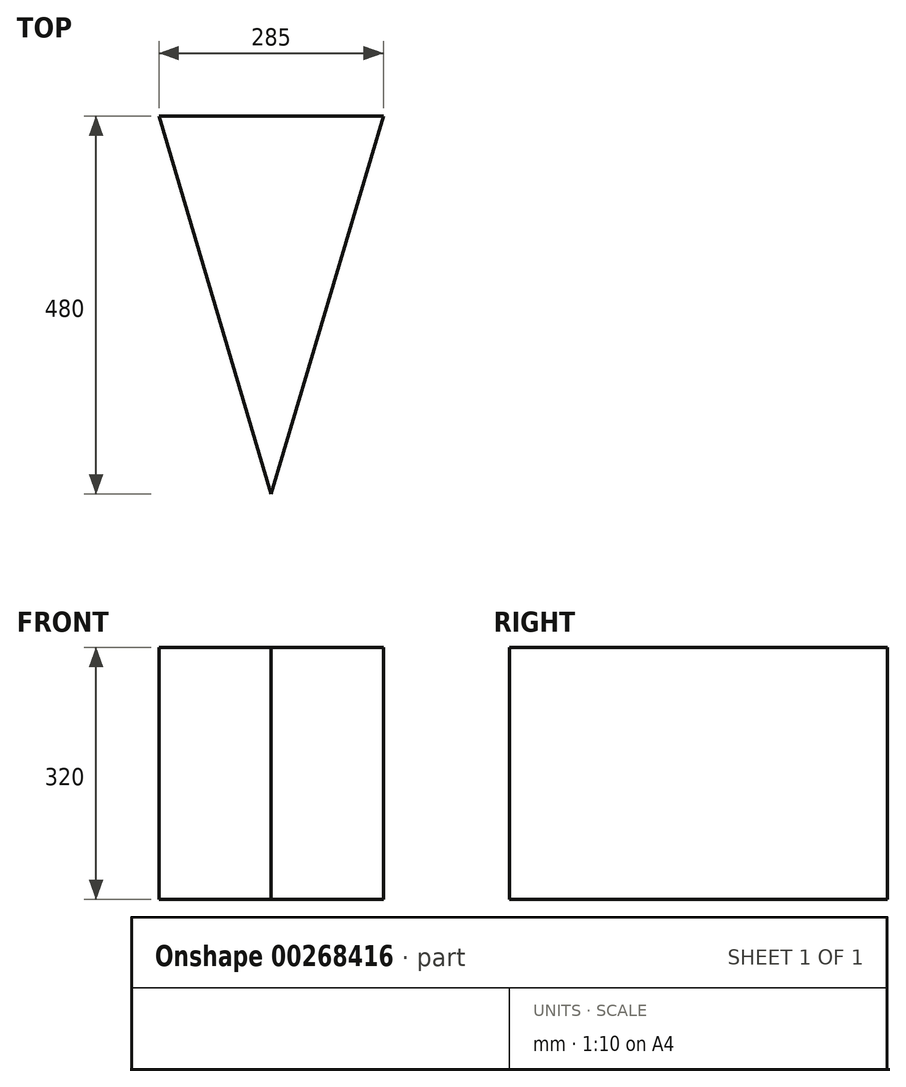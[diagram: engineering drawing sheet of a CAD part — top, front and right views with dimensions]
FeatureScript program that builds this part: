
annotation { "Feature Type Name" : "Feature", "Feature Type Description" : "" }
export const myFeature = defineFeature(function(context is Context, id is Id, definition is map)
    precondition{}
    {
        {
            var Q0;
            Q0=qCreatedBy(makeId("Top.planeOp"),FACE);
            var sketch = newSketch(context, id + "F0", { "sketchPlane" : qUnion([Q0])});
            skLineSegment(sketch, "E0.bottom", {"start": v(142.5, 240) * mm, "end": v(-142.5, 240) * mm});
            skLineSegment(sketch, "E0.top", {"start": v(142.5, -240) * mm, "end": v(-142.5, -240) * mm, "construction": true});
            skLineSegment(sketch, "E0.left", {"start": v(142.5, 240) * mm, "end": v(142.5, -240) * mm, "construction": true});
            skLineSegment(sketch, "E0.right", {"start": v(-142.5, 240) * mm, "end": v(-142.5, -240) * mm, "construction": true});
            skPoint(sketch, "E0.middle", {"position": v(0, 0) * mm});
            skLineSegment(sketch, "E1", {"start": v(0, -240) * mm, "end": v(0, 0) * mm, "construction": true});
            skLineSegment(sketch, "E2", {"start": v(0, -240) * mm, "end": v(142.5, 240) * mm});
            skLineSegment(sketch, "E3", {"start": v(0, -240) * mm, "end": v(-142.5, 240) * mm});
            skSolve(sketch);
        }
        {
            var Q0;
            Q0=makeQuery(id+"F0.imprint","IMPRINT",FACE,{"disambiguationData":[TD([[makeQuery(id+"F0.imprint","IMPRINT",EDGE,{"derivedFrom":sQuery(id+"F0.wireOp",EDGE,"E0.bottom")}),1.0]])]});
            extrude(context, id + "F1", {"entities" : qUnion([Q0]), "depth" : 320 * mm});
        }
    });
